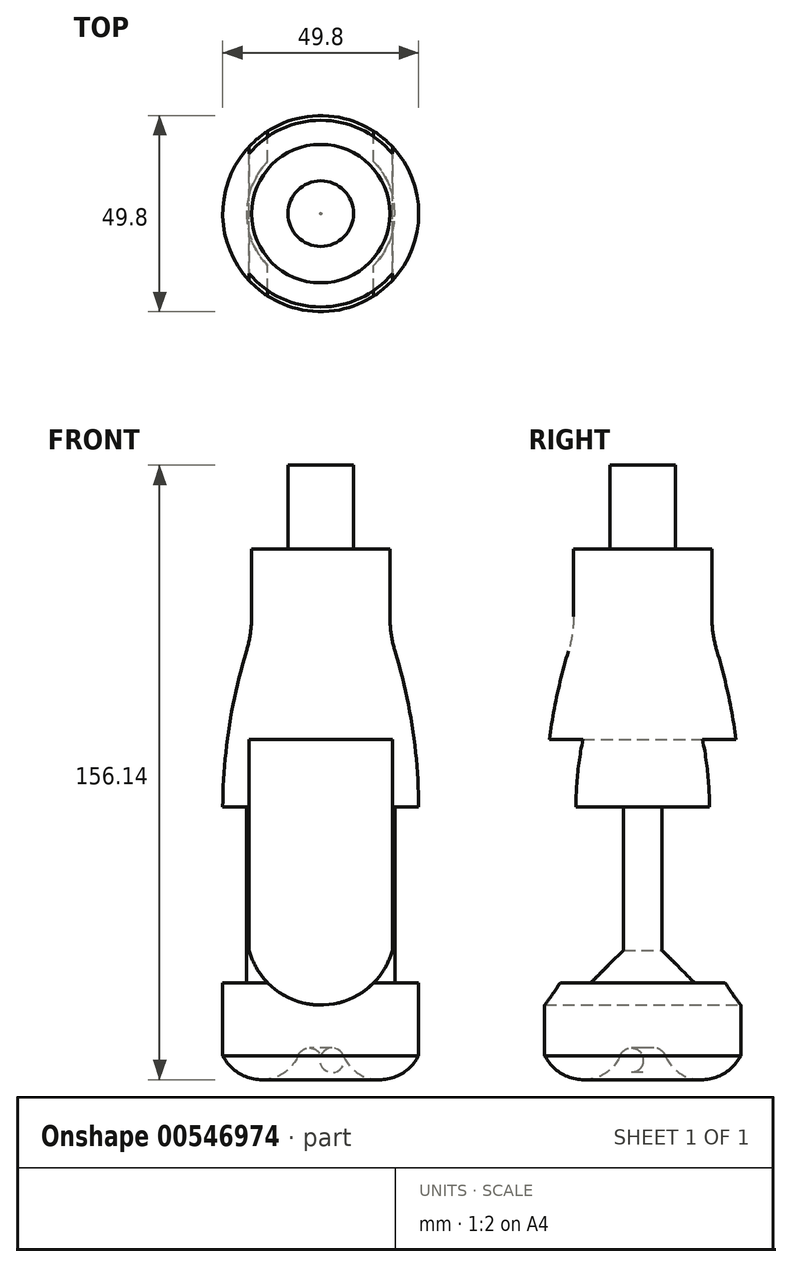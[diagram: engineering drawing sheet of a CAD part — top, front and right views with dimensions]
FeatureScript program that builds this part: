
annotation { "Feature Type Name" : "Feature", "Feature Type Description" : "" }
export const myFeature = defineFeature(function(context is Context, id is Id, definition is map)
    precondition{}
    {
        {
            var Q0;
            Q0=qCreatedBy(makeId("Front.planeOp"),FACE);
            var sketch = newSketch(context, id + "F0", { "sketchPlane" : qUnion([Q0])});
            skLineSegment(sketch, "E0.bottom", {"start": v(24.9, 78.07) * mm, "end": v(-24.9, 78.07) * mm, "construction": true});
            skLineSegment(sketch, "E0.top", {"start": v(24.9, -78.07) * mm, "end": v(-24.9, -78.07) * mm, "construction": true});
            skLineSegment(sketch, "E0.left", {"start": v(24.9, 78.07) * mm, "end": v(24.9, -78.07) * mm, "construction": true});
            skLineSegment(sketch, "E0.right", {"start": v(-24.9, 78.07) * mm, "end": v(-24.9, -78.07) * mm, "construction": true});
            skPoint(sketch, "E0.middle", {"position": v(0, 0) * mm});
            skLineSegment(sketch, "E1", {"start": v(-8.32, 78.07) * mm, "end": v(-8.32, 56.81) * mm});
            skLineSegment(sketch, "E2", {"start": v(-8.32, 56.81) * mm, "end": v(-17.58, 56.81) * mm});
            skLineSegment(sketch, "E3", {"start": v(-17.58, 56.81) * mm, "end": v(-17.58, 39.56) * mm});
            skArc(sketch, "E4", {"start": v(-17.58, 39.56) * mm, "mid": v(-17.9, 35.13) * mm, "end": v(-18.88, 30.8) * mm});
            skArc(sketch, "E5", {"start": v(-18.88, 30.8) * mm, "mid": v(-23.31, 11.2) * mm, "end": v(-24.9, -8.84) * mm});
            skLineSegment(sketch, "E6", {"start": v(-24.9, -8.84) * mm, "end": v(-18.84, -8.84) * mm});
            skLineSegment(sketch, "E7", {"start": v(-18.84, -8.84) * mm, "end": v(-18.84, -53.44) * mm});
            skLineSegment(sketch, "E8", {"start": v(-18.84, -53.44) * mm, "end": v(-24.9, -53.44) * mm});
            skLineSegment(sketch, "E9", {"start": v(-24.9, -53.44) * mm, "end": v(-24.9, -71.96) * mm});
            skLineSegment(sketch, "E10", {"start": v(-24.9, -71.96) * mm, "end": v(-24.9, -71.96) * mm});
            skArc(sketch, "E11", {"start": v(-24.9, -71.96) * mm, "mid": v(-20.64, -76.49) * mm, "end": v(-14.64, -78.07) * mm});
            skArc(sketch, "E12", {"start": v(-14.64, -78.07) * mm, "mid": v(-9.29, -76.34) * mm, "end": v(-5.76, -71.96) * mm});
            skArc(sketch, "E13", {"start": v(-5.76, -71.96) * mm, "mid": v(-2.88, -70.02) * mm, "end": v(0, -71.96) * mm});
            skLineSegment(sketch, "E14", {"start": v(-8.32, 78.07) * mm, "end": v(0, 78.07) * mm});
            skLineSegment(sketch, "E15", {"start": v(0, 78.07) * mm, "end": v(0, -71.96) * mm});
            skSolve(sketch);
        }
        {
            var Q0;
            Q0 = qSketchRegion(id + "F0", true);
            var Q1;
            Q1=sQuery(id+"F0.wireOp",EDGE,"E15");
            revolve(context, id + "F1", {"entities" : qUnion([Q0]), "axis" : qUnion([Q1]), "revolveType" : RevolveType.FULL});
        }
        {
            var Q0;
            Q0=qCreatedBy(makeId("Front.planeOp"),FACE);
            var sketch = newSketch(context, id + "F2", { "sketchPlane" : qUnion([Q0])});
            skLineSegment(sketch, "E16.bottom", {"start": v(18.2, 8.35) * mm, "end": v(-18.2, 8.35) * mm});
            skLineSegment(sketch, "E16.left", {"start": v(18.2, 8.35) * mm, "end": v(18.2, -64.8) * mm});
            skLineSegment(sketch, "E16.right", {"start": v(-18.2, 8.35) * mm, "end": v(-18.2, -64.8) * mm});
            skLineSegment(sketch, "E17", {"start": v(18.2, -45.17) * mm, "end": v(-18.2, -45.17) * mm});
            skArc(sketch, "E18", {"start": v(-18.2, -45.17) * mm, "mid": v(0, -59.1) * mm, "end": v(18.2, -45.17) * mm});
            skLineSegment(sketch, "E19", {"start": v(0, 17.2) * mm, "end": v(0, -71.3) * mm, "construction": true});
            skSolve(sketch);
        }
        {
            var Q0;
            Q0 = qSketchRegion(id + "F2", true);
            extrude(context, id + "F3", {"entities" : qUnion([Q0]), "operationType" : NewBodyOperationType.REMOVE, "endBound" : BoundingType.SYMMETRIC, "depth" : 2540 * mm, "offsetDistance" : 25.4 * mm});
        }
    });
